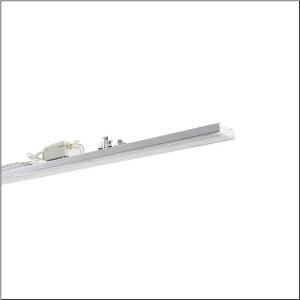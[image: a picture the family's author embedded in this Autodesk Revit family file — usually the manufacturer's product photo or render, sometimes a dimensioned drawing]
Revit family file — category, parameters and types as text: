
# Revit family: licross_11_recessed_ho_51te18dv4l5m
name_source: partatom
category: Lighting Fixtures
units: mm (PartAtom-declared; Revit-internal decimal feet)

## family parameters
Cut with Voids When Loaded = No
Host = Face
Light Source = No
Part Type = Normal
Room Calculation Point = No
Round Connector Dimension = Use Diameter
Shared = No

## types (1)
- --- (1 x LED, 20760 lm, 111.8 W, 4000K)
    Apparent Load = 112 VA
    CIE Flux Codes = 78 94 99 100 100
    Color Rendering = 80
    Color Temperature = 4000K
    Default Elevation = 1800 mm
    Description = Licross 11 Recessed HO, luminaire insert, of sheet steel, galvanised, coil coated, white, length: 2.250mm, width: 66mm, height: 67mm, LED rated luminous flux: 20.760lm, light colour: 840, SDCM (Standard Deviation of Colour Matching)MacAdam ≤ 2 SDCM (initial), control gear: DALI 2, with plug, 5-pole, with phase selection, mains connection: 220..240V, AC, 50/60Hz, rated input power: 112W, internal wiring halogen-free, primary light control with lens, of plastic, primary optical cover: cover, of PMMA, light emission: direct distribution, primary light characteristic: symmetric, protection rating (complete): IP54, insulation class (complete): insulation class I (protective earthing), certification: CE, ENEC, VDE, UKCA, protection symbol: D if used in an environment with non-conductive dust loads with corresponding accessories, impact resistance: IK06, permissible ambient temperature for indoor applications: -40..+45°C, corresponds to IFS (International Featured Standards) requirements for safety and quality in the food industry, reducing of maximum allowable ambient temperature of 5°C with ceiling mounting, LABS conformity tested according to VDMA 24364:2018-05, The light source and the operating device comply with the requirements of the Ecodesign Regulation (EU) 2019/2020 and are replaceable in accordance with this regulation, packaging unit: 1 piece
    Height = 58 mm
    Lamp = 1 x LED
    Lamp Light Flux = 20760 lm
    Lamp Power = 111.8 W
    Lamp count = 1
    Length = 2250 mm
    Luminous efficacy = 186 lm/W
    Manufacturer = Siteco
    ModVariant = No
    Model = 51TE18DV4L5M
    Mounting Place = Ceiling
    Mounting Type = Pendant
    Number of Poles = 1
    OnlyDefault = Yes
    Power Factor = 1
    Product Name = Licross 11 Recessed HO
    Product group = luminaire insert | ceiling pendant
    ProductGroupID = 901
    Protection Class = Protection class I
    Protection Degree = IP 54
    RLX_Detail_Level = 1
    RLX_Emergency_Light_Flux = 0 lm
    RLX_Emergency_Type = 0
    RLX_Emergency_Type_DB = No
    RlxData = <blob elided: 30113 chars, md5=08ca1570>
    Socket = socket
    Standby Power = 0 W
    System Light Flux = 20760 lm
    System Power = 112 W
    Type Comments = factory setting: luminous flux: 100 % | dim-lin: 254 | 520 mA
    Type Image = l_1296930.jpg
    URL = http://relux.com
    VarID = @adj_102415
    Voltage = 0 V
    Weight = 0.00 kg
    Width = 66 mm

## geometry (parser evidence)
native form markers: Blend x4, Sweep x10
no freeform markers — native parametric forms only
